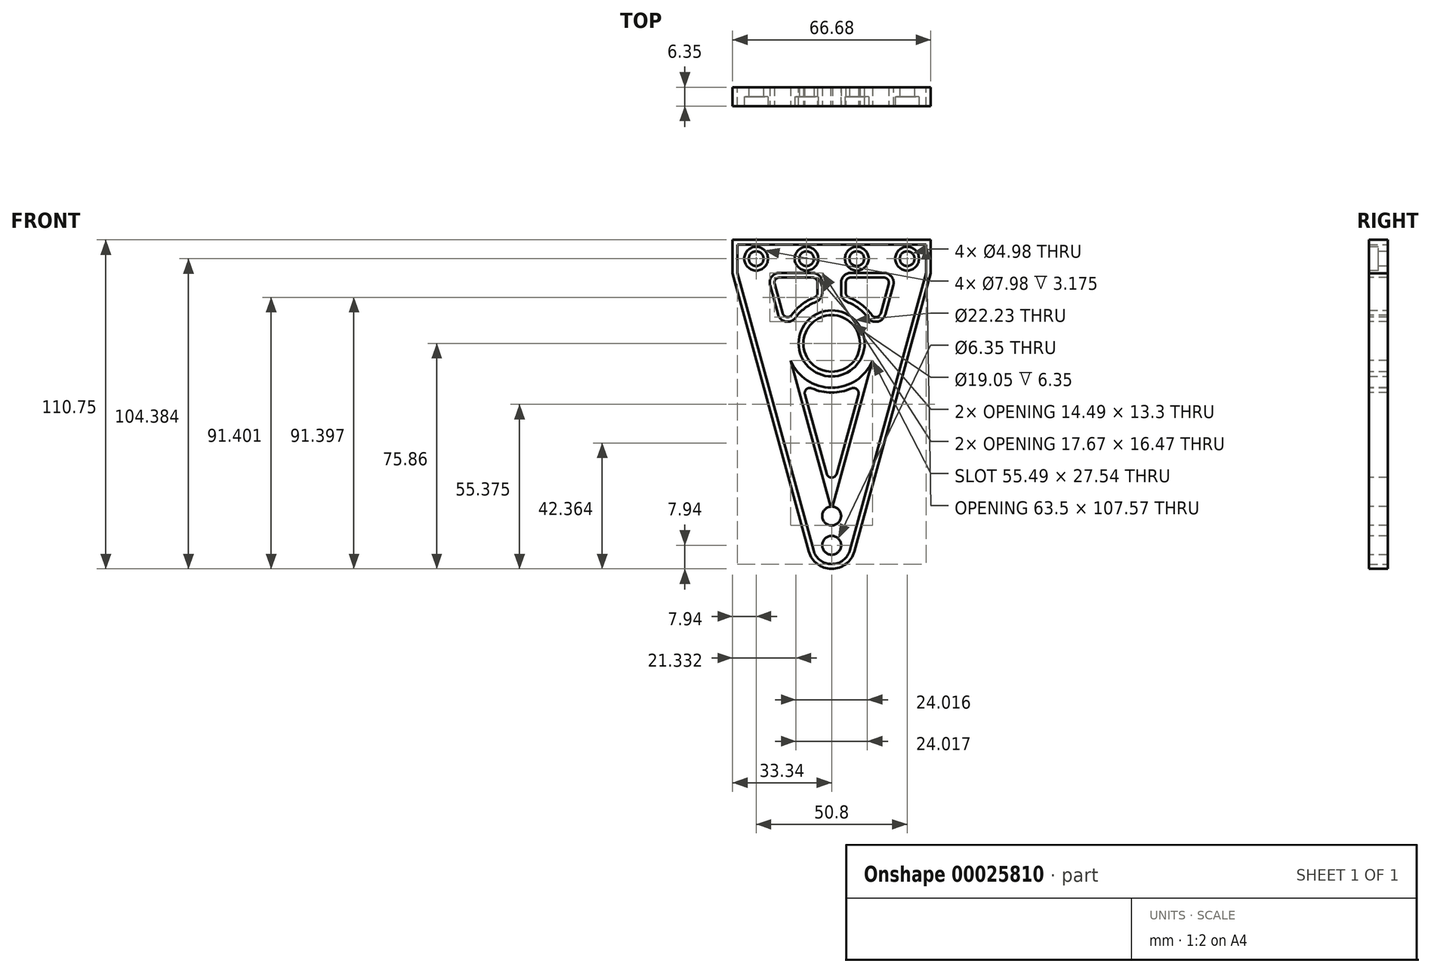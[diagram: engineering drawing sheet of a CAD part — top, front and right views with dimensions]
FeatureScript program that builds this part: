
annotation { "Feature Type Name" : "Feature", "Feature Type Description" : "" }
export const myFeature = defineFeature(function(context is Context, id is Id, definition is map)
    precondition{}
    {
        {
            var Q0;
            Q0=qCreatedBy(makeId("Front.planeOp"),FACE);
            var sketch = newSketch(context, id + "F0", { "sketchPlane" : qUnion([Q0])});
            skCircle(sketch, "E0", {"center": v(0, 0) * mm, "radius": 11.11 * mm});
            skLineSegment(sketch, "E1", {"start": v(0, 49.42) * mm, "end": v(0, 0) * mm, "construction": true});
            skLineSegment(sketch, "E2", {"start": v(47.24, 0) * mm, "end": v(0, 0) * mm, "construction": true});
            skLineSegment(sketch, "E3", {"start": v(-31.75, 33.3) * mm, "end": v(31.75, 33.3) * mm});
            skLineSegment(sketch, "E4", {"start": v(31.75, 33.3) * mm, "end": v(31.75, 23.77) * mm});
            skLineSegment(sketch, "E5", {"start": v(31.75, 23.77) * mm, "end": v(6.12, -69.6) * mm});
            skLineSegment(sketch, "E6", {"start": v(-6.12, -69.6) * mm, "end": v(-31.75, 23.77) * mm});
            skLineSegment(sketch, "E7", {"start": v(-31.75, 23.77) * mm, "end": v(-31.75, 33.3) * mm});
            skArc(sketch, "E8", {"start": v(-6.12, -69.6) * mm, "mid": v(0, -74.27) * mm, "end": v(6.12, -69.6) * mm});
            skPoint(sketch, "E9", {"position": v(0, -74.27) * mm});
            skSolve(sketch);
        }
        {
            var Q0;
            Q0=makeQuery(id+"F0.imprint","IMPRINT",FACE,{"disambiguationData":[TD([[makeQuery(id+"F0.imprint","IMPRINT",EDGE,{"derivedFrom":sQuery(id+"F0.wireOp",EDGE,"E0")}),-1.0]])]});
            var Q1;
            {var subQ5=sQuery(id+"F0.wireOp",EDGE,"E3");Q1=makeQuery(id+"F0.imprint","IMPRINT",FACE,{"disambiguationData":[TD([[makeQuery(id+"F0.imprint","IMPRINT",EDGE,{"derivedFrom":subQ5}),-1.0]])]});}
            extrude(context, id + "F1", {"entities" : qUnion([Q0, Q1]), "depth" : 6.35 * mm});
        }
        {
            var Q0;
            Q0=qCreatedBy(makeId("Front.planeOp"),FACE);
            var sketch = newSketch(context, id + "F2", { "sketchPlane" : qUnion([Q0])});
            skLineSegment(sketch, "E10.0", {"start": v(-21.87, 23.77) * mm, "end": v(-3.17, 23.77) * mm});
            skLineSegment(sketch, "E10.2", {"start": v(0, -55.92) * mm, "end": v(-13.77, -5.75) * mm});
            skLineSegment(sketch, "E10.3", {"start": v(21.87, 23.77) * mm, "end": v(14.78, -2.08) * mm});
            skArc(sketch, "E11", {"start": v(-13.77, -5.75) * mm, "mid": v(0, -14.92) * mm, "end": v(13.77, -5.75) * mm});
            skArc(sketch, "E12.trimOffspring", {"start": v(14.78, -2.08) * mm, "mid": v(12.25, 8.53) * mm, "end": v(3.17, 14.58) * mm});
            skLineSegment(sketch, "E13.trimOffspring", {"start": v(13.77, -5.75) * mm, "end": v(0, -55.92) * mm});
            skLineSegment(sketch, "E14.trimOffspring", {"start": v(-14.78, -2.08) * mm, "end": v(-21.87, 23.77) * mm});
            skLineSegment(sketch, "E15", {"start": v(0, 0) * mm, "end": v(0, 37.9) * mm, "construction": true});
            skCircle(sketch, "E16", {"center": v(0, -49.68) * mm, "radius": 1.65 * mm});
            skLineSegment(sketch, "E17", {"start": v(3.17, 14.58) * mm, "end": v(3.17, 23.77) * mm});
            skLineSegment(sketch, "E18.trimOffspring", {"start": v(3.17, 23.77) * mm, "end": v(21.87, 23.77) * mm});
            skArc(sketch, "E19.trimOffspring", {"start": v(-3.17, 14.58) * mm, "mid": v(-12.25, 8.53) * mm, "end": v(-14.78, -2.08) * mm});
            skLineSegment(sketch, "E20.trimOffspring", {"start": v(-3.17, 23.77) * mm, "end": v(-3.17, 14.58) * mm});
            skSolve(sketch);
        }
        {
            var Q0;
            Q0=qSketchRegion(id+"F2",true);
            extrude(context, id + "F3", {"entities" : qUnion([Q0]), "operationType" : NewBodyOperationType.ADD, "depth" : 25.4 * mm});
        }
        {
            var Q0;
            Q0=makeQuery(id+"F3.opExtrude","CAP_FACE",FACE,{"disambiguationData":[OSD([sQuery(id+"F2.wireOp",EDGE,"E10.0"),sQuery(id+"F2.wireOp",EDGE,"E14.trimOffspring"),sQuery(id+"F2.wireOp",EDGE,"E19.trimOffspring"),sQuery(id+"F2.wireOp",EDGE,"E20.trimOffspring")])],"isStart":false});
            var Q1;
            Q1=makeQuery(id+"F3.opExtrude","CAP_FACE",FACE,{"disambiguationData":[OSD([sQuery(id+"F2.wireOp",EDGE,"E10.3"),sQuery(id+"F2.wireOp",EDGE,"E12.trimOffspring"),sQuery(id+"F2.wireOp",EDGE,"E17"),sQuery(id+"F2.wireOp",EDGE,"E18.trimOffspring")])],"isStart":false});
            extrude(context, id + "F4", {"entities" : qUnion([Q0, Q1]), "operationType" : NewBodyOperationType.REMOVE, "oppositeDirection" : true, "depth" : 25.4 * mm});
        }
        {
            var Q0;
            Q0=makeQuery(id+"F3.opExtrude","CAP_FACE",FACE,{"disambiguationData":[OSD([sQuery(id+"F2.wireOp",EDGE,"E10.2"),sQuery(id+"F2.wireOp",EDGE,"E11"),sQuery(id+"F2.wireOp",EDGE,"E13.trimOffspring")])],"isStart":false});
            var Q1;
            Q1=qSketchRegion(id+"F2",true);
            extrude(context, id + "F5", {"entities" : qUnion([Q0, Q1]), "operationType" : NewBodyOperationType.REMOVE, "oppositeDirection" : true, "depth" : 25.4 * mm});
        }
        {
            var Q0;
            Q0=makeQuery(id+"F4.boolean.opBoolean","COPY",EDGE,{"derivedFrom":makeQuery(id+"F4.opExtrude","SWEPT_EDGE",EDGE,{"disambiguationData":[OSD([sQuery(id+"F2.wireOp",EDGE,"E10.0"),sQuery(id+"F2.wireOp",EDGE,"E14.trimOffspring")])]})});
            var Q1;
            Q1=makeQuery(id+"F4.boolean.opBoolean","COPY",EDGE,{"derivedFrom":makeQuery(id+"F4.opExtrude","SWEPT_EDGE",EDGE,{"disambiguationData":[OSD([sQuery(id+"F2.wireOp",EDGE,"E17"),sQuery(id+"F2.wireOp",EDGE,"E18.trimOffspring")])]})});
            var Q2;
            Q2=makeQuery(id+"F4.boolean.opBoolean","COPY",EDGE,{"derivedFrom":makeQuery(id+"F4.opExtrude","SWEPT_EDGE",EDGE,{"disambiguationData":[OSD([sQuery(id+"F2.wireOp",EDGE,"E10.3"),sQuery(id+"F2.wireOp",EDGE,"E18.trimOffspring")])]})});
            var Q3;
            Q3=makeQuery(id+"F4.boolean.opBoolean","COPY",EDGE,{"derivedFrom":makeQuery(id+"F4.opExtrude","SWEPT_EDGE",EDGE,{"disambiguationData":[OSD([sQuery(id+"F2.wireOp",EDGE,"E10.0"),sQuery(id+"F2.wireOp",EDGE,"E20.trimOffspring")])]})});
            var Q4;
            Q4=makeQuery(id+"F4.boolean.opBoolean","COPY",EDGE,{"derivedFrom":makeQuery(id+"F4.opExtrude","SWEPT_EDGE",EDGE,{"disambiguationData":[OSD([sQuery(id+"F2.wireOp",EDGE,"E12.trimOffspring"),sQuery(id+"F2.wireOp",EDGE,"E17")])]})});
            var Q5;
            Q5=makeQuery(id+"F4.boolean.opBoolean","COPY",EDGE,{"derivedFrom":makeQuery(id+"F4.opExtrude","SWEPT_EDGE",EDGE,{"disambiguationData":[OSD([sQuery(id+"F2.wireOp",EDGE,"E19.trimOffspring"),sQuery(id+"F2.wireOp",EDGE,"E20.trimOffspring")])]})});
            var Q6;
            Q6=makeQuery(id+"F4.boolean.opBoolean","COPY",EDGE,{"derivedFrom":makeQuery(id+"F4.opExtrude","SWEPT_EDGE",EDGE,{"disambiguationData":[OSD([sQuery(id+"F2.wireOp",EDGE,"E10.3"),sQuery(id+"F2.wireOp",EDGE,"E12.trimOffspring")])]})});
            var Q7;
            Q7=makeQuery(id+"F4.boolean.opBoolean","COPY",EDGE,{"derivedFrom":makeQuery(id+"F4.opExtrude","SWEPT_EDGE",EDGE,{"disambiguationData":[OSD([sQuery(id+"F2.wireOp",EDGE,"E14.trimOffspring"),sQuery(id+"F2.wireOp",EDGE,"E19.trimOffspring")])]})});
            var Q8;
            {var subQ0=sQuery(id+"F2.wireOp",EDGE,"E11");var subQ1=sQuery(id+"F2.wireOp",EDGE,"E13.trimOffspring");Q8=makeQuery(id+"F5.boolean.opBoolean","TWEAK_EDGE",EDGE,{"derivedFrom":[makeQuery(id+"F5.opExtrude","SWEPT_EDGE",EDGE,{"disambiguationData":[OSD([subQ0,subQ1]),TDD([makeQuery(id+"F2.imprint","INTERSECT",VERTEX,{"derivedFrom":[subQ0,subQ1]})])]}),makeQuery(id+"F5.opExtrude","SWEPT_EDGE",EDGE,{"disambiguationData":[OSD([subQ0,subQ1]),TDD([makeQuery(id+"F3.opExtrude","CAP_VERTEX",VERTEX,{"disambiguationData":[OSD([subQ0,subQ1])],"isStart":false})])]})]});}
            var Q9;
            {var subQ0=sQuery(id+"F2.wireOp",EDGE,"E10.2");var subQ1=sQuery(id+"F2.wireOp",EDGE,"E11");Q9=makeQuery(id+"F5.boolean.opBoolean","TWEAK_EDGE",EDGE,{"derivedFrom":[makeQuery(id+"F5.opExtrude","SWEPT_EDGE",EDGE,{"disambiguationData":[OSD([subQ0,subQ1]),TDD([makeQuery(id+"F2.imprint","INTERSECT",VERTEX,{"derivedFrom":[subQ0,subQ1]})])]}),makeQuery(id+"F5.opExtrude","SWEPT_EDGE",EDGE,{"disambiguationData":[OSD([subQ0,subQ1]),TDD([makeQuery(id+"F3.opExtrude","CAP_VERTEX",VERTEX,{"disambiguationData":[OSD([subQ0,subQ1])],"isStart":false})])]})]});}
            var Q10;
            {var subQ0=sQuery(id+"F2.wireOp",EDGE,"E10.2");var subQ1=sQuery(id+"F2.wireOp",EDGE,"E13.trimOffspring");Q10=makeQuery(id+"F5.boolean.opBoolean","TWEAK_EDGE",EDGE,{"derivedFrom":[makeQuery(id+"F5.opExtrude","SWEPT_EDGE",EDGE,{"disambiguationData":[OSD([subQ0,subQ1]),TDD([makeQuery(id+"F2.imprint","INTERSECT",VERTEX,{"derivedFrom":[subQ0,subQ1]})])]}),makeQuery(id+"F5.opExtrude","SWEPT_EDGE",EDGE,{"disambiguationData":[OSD([subQ0,subQ1]),TDD([makeQuery(id+"F3.opExtrude","CAP_VERTEX",VERTEX,{"disambiguationData":[OSD([subQ0,subQ1])],"isStart":false})])]})]});}
            fillet(context, id + "F6", {"entities" : qUnion([Q0, Q1, Q2, Q3, Q4, Q5, Q6, Q7, Q8, Q9, Q10]), "radius" : 3.3 * mm, "tangentPropagation" : true, "allowEdgeOverflow" : false});
        }
        {
            var Q0;
            Q0=makeQuery(id+"F1.opExtrude","CAP_FACE",FACE,{"disambiguationData":[OSD([sQuery(id+"F0.wireOp",EDGE,"E0"),sQuery(id+"F0.wireOp",EDGE,"E3"),sQuery(id+"F0.wireOp",EDGE,"E4"),sQuery(id+"F0.wireOp",EDGE,"E5"),sQuery(id+"F0.wireOp",EDGE,"E6"),sQuery(id+"F0.wireOp",EDGE,"E7"),sQuery(id+"F0.wireOp",EDGE,"E8")])],"isStart":false});
            var sketch = newSketch(context, id + "F7", { "sketchPlane" : qUnion([Q0])});
            skLineSegment(sketch, "E21", {"start": v(-32.96, 28.52) * mm, "end": v(70.24, 28.52) * mm});
            skPoint(sketch, "E22", {"position": v(-25.4, 28.52) * mm});
            skPoint(sketch, "E23", {"position": v(-8.46, 28.52) * mm});
            skPoint(sketch, "E24", {"position": v(8.46, 28.52) * mm});
            skPoint(sketch, "E25", {"position": v(25.4, 28.52) * mm});
            skSolve(sketch);
        }
        {
            var Q0;
            Q0=sQuery(id+"F7.wireOp",VERTEX,"E22");
            var Q1;
            Q1=sQuery(id+"F7.wireOp",VERTEX,"E23");
            var Q2;
            Q2=sQuery(id+"F7.wireOp",VERTEX,"E24");
            var Q3;
            Q3=sQuery(id+"F7.wireOp",VERTEX,"E25");
            var Q4;
            Q4=makeQuery(id+"F1.opExtrude","SWEPT_BODY",BODY,{"disambiguationData":[OSD([sQuery(id+"F0.wireOp",EDGE,"E0"),sQuery(id+"F0.wireOp",EDGE,"E3"),sQuery(id+"F0.wireOp",EDGE,"E4"),sQuery(id+"F0.wireOp",EDGE,"E5"),sQuery(id+"F0.wireOp",EDGE,"E6"),sQuery(id+"F0.wireOp",EDGE,"E7"),sQuery(id+"F0.wireOp",EDGE,"E8")])]});
            hole(context, id + "F8", {"style" : HoleStyle.C_BORE, "holeDiameter" : 4.98 * mm, "cBoreDiameter" : 7.98 * mm, "cBoreDepth" : 3.17 * mm, "endStyle" : HoleEndStyle.THROUGH, "locations" : qUnion([Q0, Q1, Q2, Q3]), "scope" : qUnion([Q4])});
        }
        {
            var Q0;
            Q0=makeQuery(id+"F1.opExtrude","CAP_FACE",FACE,{"disambiguationData":[OSD([sQuery(id+"F0.wireOp",EDGE,"E0"),sQuery(id+"F0.wireOp",EDGE,"E3"),sQuery(id+"F0.wireOp",EDGE,"E4"),sQuery(id+"F0.wireOp",EDGE,"E5"),sQuery(id+"F0.wireOp",EDGE,"E6"),sQuery(id+"F0.wireOp",EDGE,"E7"),sQuery(id+"F0.wireOp",EDGE,"E8")])],"isStart":false});
            var sketch = newSketch(context, id + "F9", { "sketchPlane" : qUnion([Q0])});
            skLineSegment(sketch, "E26", {"start": v(0, 37.58) * mm, "end": v(0, -79.68) * mm});
            skPoint(sketch, "E27", {"position": v(0, -58.06) * mm});
            skPoint(sketch, "E28", {"position": v(0, -67.92) * mm});
            skSolve(sketch);
        }
        {
            var Q0;
            Q0=sQuery(id+"F9.wireOp",VERTEX,"E27");
            var Q1;
            Q1=sQuery(id+"F9.wireOp",VERTEX,"E28");
            var Q2;
            Q2=makeQuery(id+"F1.opExtrude","SWEPT_BODY",BODY,{"disambiguationData":[OSD([sQuery(id+"F0.wireOp",EDGE,"E0"),sQuery(id+"F0.wireOp",EDGE,"E3"),sQuery(id+"F0.wireOp",EDGE,"E4"),sQuery(id+"F0.wireOp",EDGE,"E5"),sQuery(id+"F0.wireOp",EDGE,"E6"),sQuery(id+"F0.wireOp",EDGE,"E7"),sQuery(id+"F0.wireOp",EDGE,"E8")])]});
            hole(context, id + "F10", {"style" : HoleStyle.SIMPLE, "holeDiameter" : 6.35 * mm, "endStyle" : HoleEndStyle.THROUGH, "locations" : qUnion([Q0, Q1]), "scope" : qUnion([Q2])});
        }
        {
            var Q0;
            Q0=makeQuery(id+"F1.opExtrude","CAP_FACE",FACE,{"disambiguationData":[OSD([sQuery(id+"F0.wireOp",EDGE,"E0"),sQuery(id+"F0.wireOp",EDGE,"E3"),sQuery(id+"F0.wireOp",EDGE,"E4"),sQuery(id+"F0.wireOp",EDGE,"E5"),sQuery(id+"F0.wireOp",EDGE,"E6"),sQuery(id+"F0.wireOp",EDGE,"E7"),sQuery(id+"F0.wireOp",EDGE,"E8")])],"isStart":true});
            var sketch = newSketch(context, id + "F11", { "sketchPlane" : qUnion([Q0])});
            skSolve(sketch);
        }
        {
            var Q0;
            Q0=makeQuery(id+"F1.opExtrude","CAP_FACE",FACE,{"disambiguationData":[OSD([sQuery(id+"F0.wireOp",EDGE,"E0"),sQuery(id+"F0.wireOp",EDGE,"E3"),sQuery(id+"F0.wireOp",EDGE,"E4"),sQuery(id+"F0.wireOp",EDGE,"E5"),sQuery(id+"F0.wireOp",EDGE,"E6"),sQuery(id+"F0.wireOp",EDGE,"E7"),sQuery(id+"F0.wireOp",EDGE,"E8")])],"isStart":false});
            var sketch = newSketch(context, id + "F12", { "sketchPlane" : qUnion([Q0])});
            skLineSegment(sketch, "E29.0", {"start": v(-33.34, 34.89) * mm, "end": v(33.34, 34.89) * mm});
            skLineSegment(sketch, "E29.1", {"start": v(-33.34, 23.56) * mm, "end": v(-33.34, 34.89) * mm});
            skLineSegment(sketch, "E29.2", {"start": v(-7.65, -70.02) * mm, "end": v(-33.34, 23.56) * mm});
            skArc(sketch, "E29.3", {"start": v(-7.65, -70.02) * mm, "mid": v(0, -75.86) * mm, "end": v(7.65, -70.02) * mm});
            skLineSegment(sketch, "E29.4", {"start": v(33.34, 23.56) * mm, "end": v(7.65, -70.02) * mm});
            skLineSegment(sketch, "E29.5", {"start": v(33.34, 34.89) * mm, "end": v(33.34, 23.56) * mm});
            skLineSegment(sketch, "E30.0", {"start": v(-19.2, 20.02) * mm, "end": v(-16.48, 10.14) * mm});
            skArc(sketch, "E30.1", {"start": v(-13.44, 9.6) * mm, "mid": v(-15.13, 8.9) * mm, "end": v(-16.48, 10.14) * mm});
            skArc(sketch, "E30.2", {"start": v(-13.44, 9.6) * mm, "mid": v(-10.08, 13.07) * mm, "end": v(-5.87, 15.43) * mm});
            skArc(sketch, "E30.3", {"start": v(-4.76, 17.04) * mm, "mid": v(-5.06, 16.06) * mm, "end": v(-5.87, 15.43) * mm});
            skLineSegment(sketch, "E30.4", {"start": v(-4.76, 17.04) * mm, "end": v(-4.76, 20.47) * mm});
            skArc(sketch, "E30.5", {"start": v(-19.2, 20.02) * mm, "mid": v(-18.9, 21.51) * mm, "end": v(-17.54, 22.19) * mm});
            skArc(sketch, "E30.6", {"start": v(-6.48, 22.19) * mm, "mid": v(-5.26, 21.68) * mm, "end": v(-4.76, 20.47) * mm});
            skLineSegment(sketch, "E30.7", {"start": v(-6.48, 22.19) * mm, "end": v(-17.54, 22.19) * mm});
            skLineSegment(sketch, "E31.0", {"start": v(6.48, 22.19) * mm, "end": v(17.54, 22.19) * mm});
            skArc(sketch, "E31.1", {"start": v(4.76, 20.47) * mm, "mid": v(5.26, 21.68) * mm, "end": v(6.48, 22.19) * mm});
            skLineSegment(sketch, "E31.2", {"start": v(4.76, 17.04) * mm, "end": v(4.76, 20.47) * mm});
            skArc(sketch, "E31.3", {"start": v(5.87, 15.43) * mm, "mid": v(5.06, 16.06) * mm, "end": v(4.76, 17.04) * mm});
            skArc(sketch, "E31.4", {"start": v(13.44, 9.6) * mm, "mid": v(10.08, 13.07) * mm, "end": v(5.87, 15.43) * mm});
            skArc(sketch, "E31.5", {"start": v(17.54, 22.19) * mm, "mid": v(18.9, 21.51) * mm, "end": v(19.2, 20.02) * mm});
            skArc(sketch, "E31.6", {"start": v(16.48, 10.14) * mm, "mid": v(15.13, 8.9) * mm, "end": v(13.44, 9.6) * mm});
            skLineSegment(sketch, "E31.7", {"start": v(19.2, 20.02) * mm, "end": v(16.48, 10.14) * mm});
            skCircle(sketch, "E32.0", {"center": v(0, 0) * mm, "radius": 9.53 * mm});
            skArc(sketch, "E33.0", {"start": v(-9, -17.13) * mm, "mid": v(-8.47, -15.38) * mm, "end": v(-6.66, -15.1) * mm});
            skLineSegment(sketch, "E33.1", {"start": v(-9, -17.13) * mm, "end": v(-1.65, -43.9) * mm});
            skArc(sketch, "E33.2", {"start": v(1.65, -43.9) * mm, "mid": v(0, -45.16) * mm, "end": v(-1.65, -43.9) * mm});
            skLineSegment(sketch, "E33.3", {"start": v(1.65, -43.9) * mm, "end": v(9, -17.13) * mm});
            skArc(sketch, "E33.4", {"start": v(6.66, -15.1) * mm, "mid": v(8.47, -15.38) * mm, "end": v(9, -17.13) * mm});
            skArc(sketch, "E33.5", {"start": v(6.66, -15.1) * mm, "mid": v(0, -16.51) * mm, "end": v(-6.66, -15.1) * mm});
            skArc(sketch, "E34.0", {"start": v(-10.53, -17.55) * mm, "mid": v(-9.5, -14.18) * mm, "end": v(-6.02, -13.66) * mm});
            skLineSegment(sketch, "E35.0", {"start": v(-10.53, -17.55) * mm, "end": v(-3.18, -44.32) * mm});
            skArc(sketch, "E36.0", {"start": v(6.02, -13.66) * mm, "mid": v(0, -14.92) * mm, "end": v(-6.02, -13.66) * mm});
            skArc(sketch, "E37.0", {"start": v(6.02, -13.66) * mm, "mid": v(9.5, -14.18) * mm, "end": v(10.53, -17.55) * mm});
            skLineSegment(sketch, "E38.0", {"start": v(3.18, -44.32) * mm, "end": v(10.53, -17.55) * mm});
            skCircle(sketch, "E39.0", {"center": v(0, 0) * mm, "radius": 11.11 * mm});
            skArc(sketch, "E40.0", {"start": v(-12.14, 8.67) * mm, "mid": v(-9.11, 11.82) * mm, "end": v(-5.3, 13.95) * mm});
            skArc(sketch, "E41.0", {"start": v(-3.17, 17.04) * mm, "mid": v(-3.76, 15.16) * mm, "end": v(-5.3, 13.95) * mm});
            skLineSegment(sketch, "E42.0", {"start": v(-3.17, 17.04) * mm, "end": v(-3.17, 20.47) * mm});
            skArc(sketch, "E43.0", {"start": v(-6.48, 23.77) * mm, "mid": v(-4.14, 22.8) * mm, "end": v(-3.17, 20.47) * mm});
            skLineSegment(sketch, "E44.0", {"start": v(-6.48, 23.77) * mm, "end": v(-17.54, 23.77) * mm});
            skArc(sketch, "E45.0", {"start": v(-20.73, 19.6) * mm, "mid": v(-20.17, 22.47) * mm, "end": v(-17.54, 23.77) * mm});
            skLineSegment(sketch, "E46.0", {"start": v(-20.73, 19.6) * mm, "end": v(-18.01, 9.72) * mm});
            skArc(sketch, "E47.0", {"start": v(-12.14, 8.67) * mm, "mid": v(-15.4, 7.34) * mm, "end": v(-18.01, 9.72) * mm});
            skArc(sketch, "E48.0", {"start": v(5.3, 13.95) * mm, "mid": v(9.11, 11.82) * mm, "end": v(12.14, 8.67) * mm});
            skArc(sketch, "E49.0", {"start": v(5.3, 13.95) * mm, "mid": v(3.76, 15.16) * mm, "end": v(3.17, 17.04) * mm});
            skLineSegment(sketch, "E50.0", {"start": v(3.17, 20.47) * mm, "end": v(3.17, 17.04) * mm});
            skArc(sketch, "E51.0", {"start": v(3.17, 20.47) * mm, "mid": v(4.14, 22.8) * mm, "end": v(6.48, 23.77) * mm});
            skLineSegment(sketch, "E52.0", {"start": v(17.54, 23.77) * mm, "end": v(6.48, 23.77) * mm});
            skArc(sketch, "E53.0", {"start": v(17.54, 23.77) * mm, "mid": v(20.17, 22.47) * mm, "end": v(20.73, 19.6) * mm});
            skLineSegment(sketch, "E54.0", {"start": v(18.01, 9.72) * mm, "end": v(20.73, 19.6) * mm});
            skArc(sketch, "E55.0", {"start": v(18.01, 9.72) * mm, "mid": v(15.4, 7.34) * mm, "end": v(12.14, 8.67) * mm});
            skLineSegment(sketch, "E56.0", {"start": v(-31.75, 23.77) * mm, "end": v(-31.75, 33.3) * mm});
            skLineSegment(sketch, "E57.0", {"start": v(-31.75, 33.3) * mm, "end": v(31.75, 33.3) * mm});
            skLineSegment(sketch, "E58.0", {"start": v(31.75, 33.3) * mm, "end": v(31.75, 23.77) * mm});
            skLineSegment(sketch, "E59.0", {"start": v(31.75, 23.77) * mm, "end": v(6.12, -69.6) * mm});
            skLineSegment(sketch, "E60.0", {"start": v(-6.12, -69.6) * mm, "end": v(-31.75, 23.77) * mm});
            skArc(sketch, "E61.0", {"start": v(-6.12, -69.6) * mm, "mid": v(0, -74.27) * mm, "end": v(6.12, -69.6) * mm});
            skSolve(sketch);
        }
        {
            var Q0;
            Q0=makeQuery(id+"F12.imprint","IMPRINT",FACE,{"disambiguationData":[TD([[makeQuery(id+"F12.imprint","IMPRINT",EDGE,{"derivedFrom":sQuery(id+"F12.wireOp",EDGE,"E29.0")}),-1.0]])]});
            var Q1;
            Q1=makeQuery(id+"F12.imprint","IMPRINT",FACE,{"disambiguationData":[TD([[makeQuery(id+"F12.imprint","IMPRINT",EDGE,{"derivedFrom":sQuery(id+"F12.wireOp",EDGE,"E30.0")}),-1.0]])]});
            var Q2;
            Q2=makeQuery(id+"F12.imprint","IMPRINT",FACE,{"disambiguationData":[TD([[makeQuery(id+"F12.imprint","IMPRINT",EDGE,{"derivedFrom":sQuery(id+"F12.wireOp",EDGE,"E31.0")}),1.0]])]});
            var Q3;
            Q3=makeQuery(id+"F12.imprint","IMPRINT",FACE,{"disambiguationData":[TD([[makeQuery(id+"F12.imprint","IMPRINT",EDGE,{"derivedFrom":sQuery(id+"F12.wireOp",EDGE,"E33.0")}),1.0]])]});
            extrude(context, id + "F13", {"entities" : qUnion([Q0, Q1, Q2, Q3]), "oppositeDirection" : true, "depth" : 6.35 * mm});
        }
        {
            var Q0;
            Q0=makeQuery(id+"F1.opExtrude","CAP_FACE",FACE,{"disambiguationData":[OSD([sQuery(id+"F0.wireOp",EDGE,"E0"),sQuery(id+"F0.wireOp",EDGE,"E3"),sQuery(id+"F0.wireOp",EDGE,"E4"),sQuery(id+"F0.wireOp",EDGE,"E5"),sQuery(id+"F0.wireOp",EDGE,"E6"),sQuery(id+"F0.wireOp",EDGE,"E7"),sQuery(id+"F0.wireOp",EDGE,"E8")])],"isStart":false});
            var sketch = newSketch(context, id + "F14", { "sketchPlane" : qUnion([Q0])});
            skCircle(sketch, "E62.0", {"center": v(0, 0) * mm, "radius": 9.53 * mm});
            skCircle(sketch, "E63.0", {"center": v(0, 0) * mm, "radius": 11.11 * mm});
            skSolve(sketch);
        }
        {
            var Q0;
            Q0=makeQuery(id+"F14.imprint","IMPRINT",FACE,{"disambiguationData":[TD([[makeQuery(id+"F14.imprint","IMPRINT",EDGE,{"derivedFrom":sQuery(id+"F14.wireOp",EDGE,"E62.0")}),-1.0]])]});
            extrude(context, id + "F15", {"entities" : qUnion([Q0]), "oppositeDirection" : true, "depth" : 6.35 * mm});
        }
    });
